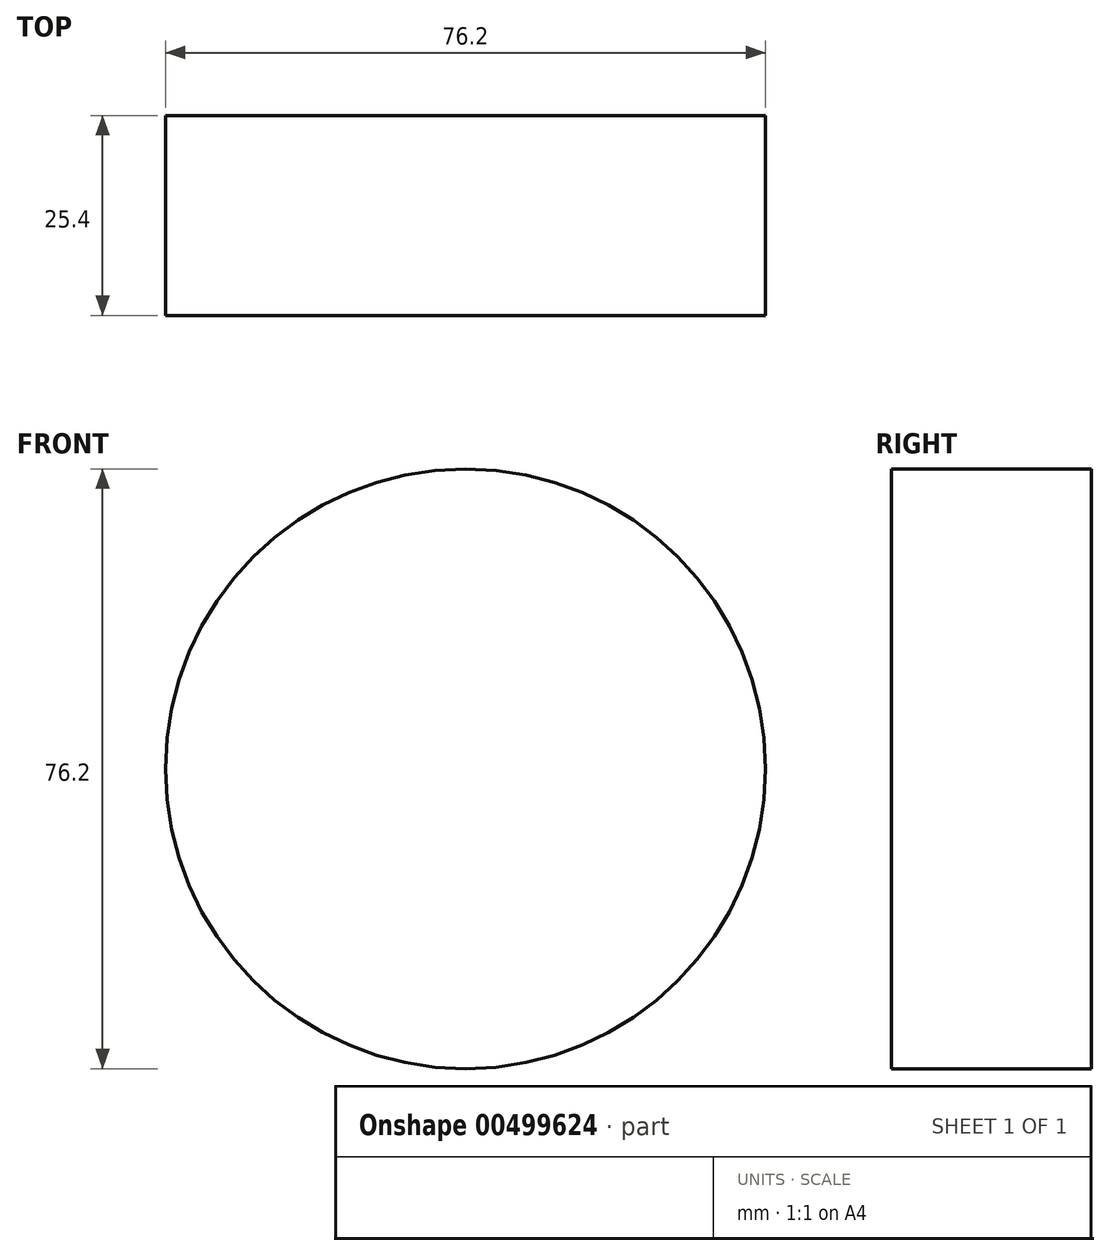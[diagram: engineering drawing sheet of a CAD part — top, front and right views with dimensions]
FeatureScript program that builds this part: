
annotation { "Feature Type Name" : "Feature", "Feature Type Description" : "" }
export const myFeature = defineFeature(function(context is Context, id is Id, definition is map)
    precondition{}
    {
        {
            var Q0;
            Q0=qCreatedBy(makeId("Front.planeOp"),FACE);
            var sketch = newSketch(context, id + "F0", { "sketchPlane" : qUnion([Q0])});
            skCircle(sketch, "E0", {"center": v(4.07, 0) * mm, "radius": 38.1 * mm});
            skSolve(sketch);
        }
        {
            var Q0;
            Q0 = qSketchRegion(id + "F0", true);
            extrude(context, id + "F1", {"entities" : qUnion([Q0]), "depth" : 25.4 * mm});
        }
    });
